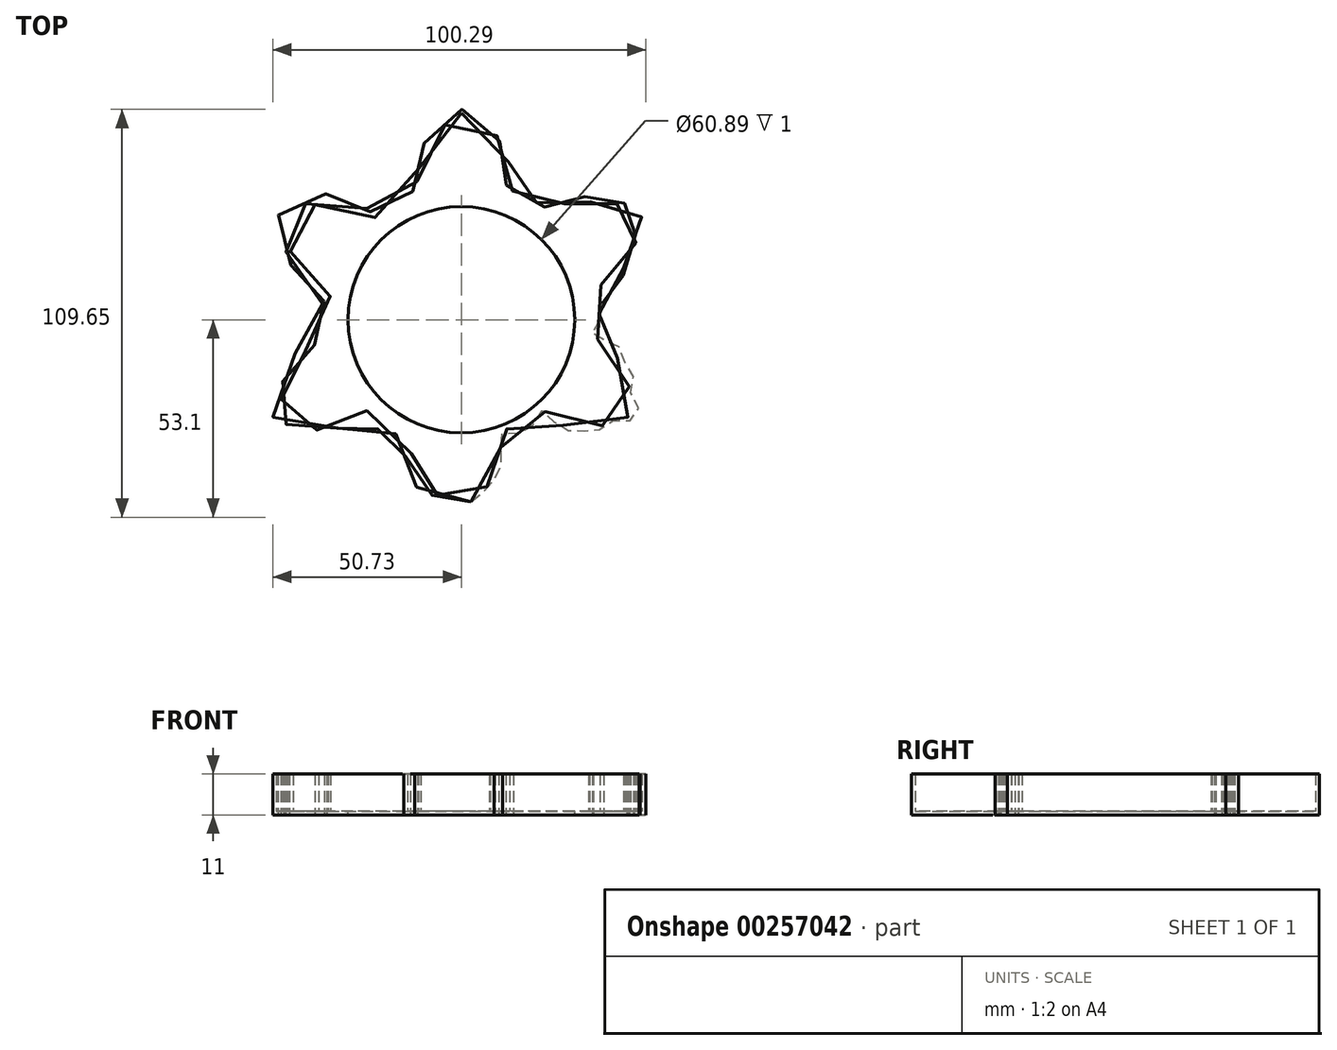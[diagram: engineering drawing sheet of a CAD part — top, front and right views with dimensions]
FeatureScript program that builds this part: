
annotation { "Feature Type Name" : "Feature", "Feature Type Description" : "" }
export const myFeature = defineFeature(function(context is Context, id is Id, definition is map)
    precondition{}
    {
        {
            var Q0;
            Q0=qCreatedBy(makeId("Top.planeOp"),FACE);
            var sketch = newSketch(context, id + "F0", { "sketchPlane" : qUnion([Q0])});
            skFitSpline(sketch, "E0", {"points": [v(0, 55.55) * mm, v(-5.87, 48.94) * mm, v(-8.32, 48.21) * mm, v(-10.28, 44.05) * mm, v(-11.5, 41.36) * mm, v(-11.25, 34.5) * mm, v(-17.37, 33.04) * mm, v(-20.55, 30.84) * mm, v(-23.73, 27.41) * mm, v(-29.6, 32.3) * mm, v(-33.27, 30.84) * mm, v(-36.45, 32.8) * mm, v(-40.12, 30.6) * mm, v(-46.49, 29.86) * mm, v(-48.2, 26.44) * mm, v(-45.26, 21.3) * mm, v(-46.24, 17.38) * mm, v(-44.53, 14.7) * mm, v(-42.08, 11.27) * mm, v(-38.66, 10.04) * mm, v(-35.23, 6.86) * mm, v(-38.41, 0) * mm, v(-36.45, -2.92) * mm, v(-36.45, -6.6) * mm, v(-41.84, -8.3) * mm, v(-44.04, -10.02) * mm, v(-45.26, -12.7) * mm, v(-47.46, -13.93) * mm, v(-46.73, -18.34) * mm, v(-48.93, -22.25) * mm, v(-49.67, -24.7) * mm, v(-49.18, -26.66) * mm, v(-42.33, -27.39) * mm, v(-40.12, -29.1) * mm, v(-37.68, -29.6) * mm, v(-35.23, -28.12) * mm, v(-32.54, -28.12) * mm, v(-29.85, -26.17) * mm, v(-27.65, -24.45) * mm, v(-24.22, -25.19) * mm, v(-20.8, -29.35) * mm, v(-14.92, -29.84) * mm, v(-12.72, -33.75) * mm, v(-14.2, -37.42) * mm, v(-14.2, -39.38) * mm, v(-11.74, -41.1) * mm, v(-11.5, -44.03) * mm, v(-8.32, -45.74) * mm, v(-5.14, -48.92) * mm, v(-2.2, -52.1) * mm, v(1.71, -48.43) * mm, v(3.91, -45.74) * mm, v(7.58, -44.52) * mm, v(7.58, -42.31) * mm, v(10.03, -37.91) * mm, v(9.05, -31.3) * mm, v(12.48, -29.35) * mm, v(17.13, -29.1) * mm, v(19.57, -25.43) * mm, v(22.26, -23.48) * mm, v(27.9, -28.61) * mm, v(31.32, -28.12) * mm, v(35.23, -29.6) * mm, v(38.41, -26.66) * mm, v(45.02, -26.17) * mm, v(46.73, -24.45) * mm, v(44.04, -18.1) * mm, v(45.26, -14.42) * mm, v(42.08, -10.75) * mm, v(41.1, -7.08) * mm, v(37.68, -6.6) * mm, v(34.25, -4.15) * mm, v(35.97, 0) * mm, v(37.19, 3.2) * mm, v(34.5, 7.84) * mm, v(35.48, 9.55) * mm, v(41.84, 12) * mm, v(43.55, 14.2) * mm, v(43.8, 16.16) * mm, v(46.98, 18.12) * mm, v(45.5, 21.05) * mm, v(46.98, 24.97) * mm, v(48.44, 28.88) * mm, v(43.8, 30.35) * mm, v(39.4, 30.84) * mm, v(37.92, 33.78) * mm, v(34.25, 31.57) * mm, v(31.8, 32.55) * mm, v(28.14, 30.1) * mm, v(25.45, 27.66) * mm, v(20.8, 30.6) * mm, v(18.84, 33.29) * mm, v(12.97, 33.78) * mm, v(11.01, 35.98) * mm, v(12.97, 41.36) * mm, v(11.5, 43.56) * mm, v(9.3, 47.72) * mm, v(8.8, 48.7) * mm, v(5.63, 49.68) * mm, v(0, 55.55) * mm]});
            skSolve(sketch);
        }
        {
            var Q0;
            Q0=makeQuery(id+"F0.imprint","IMPRINT",FACE,{"disambiguationData":[TD([[makeQuery(id+"F0.imprint","IMPRINT",EDGE,{"derivedFrom":sQuery(id+"F0.wireOp",EDGE,"E0")}),1.0]])]});
            extrude(context, id + "F1", {"entities" : qUnion([Q0]), "depth" : 10 * mm});
        }
        {
            var Q0;
            Q0=makeQuery(id+"F1.opExtrude","CAP_FACE",FACE,{"disambiguationData":[OSD([sQuery(id+"F0.wireOp",EDGE,"E0")])],"isStart":false});
            shell(context, id + "F2", {"entities" : qUnion([Q0]), "thickness" : 1 * mm, "oppositeDirection" : true});
        }
        {
            var Q0;
            {var subQ0=sQuery(id+"F0.wireOp",EDGE,"E0");Q0=makeQuery(id+"F2.opShell","OFFSET_FACE",FACE,{"disambiguationData":[OSD([subQ0]),TDD([makeQuery(id+"F1.opExtrude","CAP_FACE",FACE,{"disambiguationData":[OSD([subQ0])],"isStart":true})])]});}
            var sketch = newSketch(context, id + "F3", { "sketchPlane" : qUnion([Q0])});
            skCircle(sketch, "E1", {"center": v(0, 0) * mm, "radius": 30.45 * mm});
            skSolve(sketch);
        }
        {
            var Q0;
            Q0 = qSketchRegion(id + "F3", true);
            extrude(context, id + "F4", {"entities" : qUnion([Q0]), "operationType" : NewBodyOperationType.REMOVE, "oppositeDirection" : true, "depth" : 25 * mm});
        }
    });
